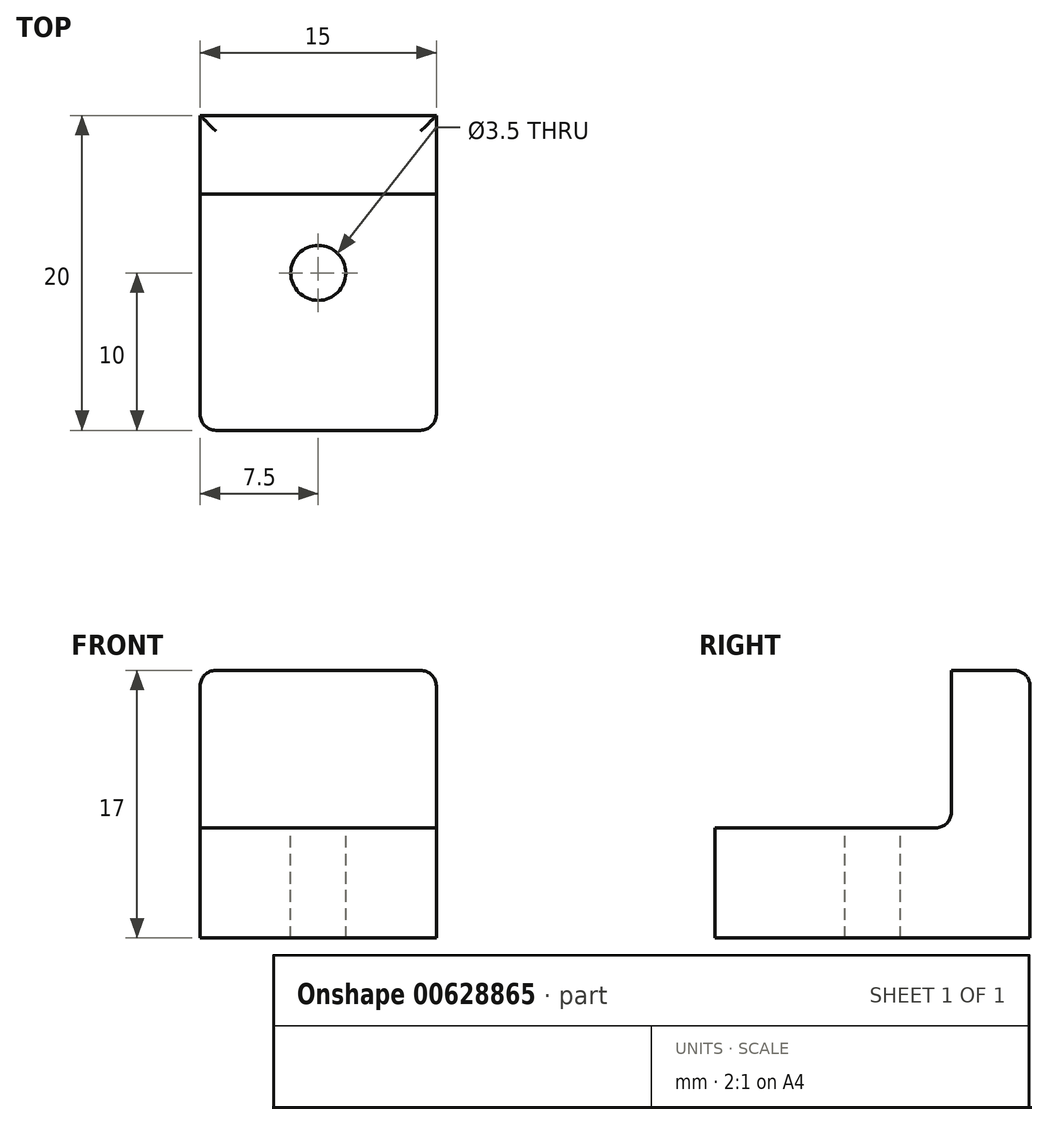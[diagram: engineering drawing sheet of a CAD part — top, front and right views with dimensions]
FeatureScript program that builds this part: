
annotation { "Feature Type Name" : "Feature", "Feature Type Description" : "" }
export const myFeature = defineFeature(function(context is Context, id is Id, definition is map)
    precondition{}
    {
        {
            var Q0;
            Q0=qCreatedBy(makeId("Top.planeOp"),FACE);
            var sketch = newSketch(context, id + "F0", { "sketchPlane" : qUnion([Q0])});
            skLineSegment(sketch, "E0.bottom", {"start": v(0, 0) * mm, "end": v(-15, 0) * mm});
            skLineSegment(sketch, "E0.top", {"start": v(0, 20) * mm, "end": v(-15, 20) * mm});
            skLineSegment(sketch, "E0.left", {"start": v(0, 0) * mm, "end": v(0, 20) * mm});
            skLineSegment(sketch, "E0.right", {"start": v(-15, 0) * mm, "end": v(-15, 20) * mm});
            skSolve(sketch);
        }
        {
            var Q0;
            Q0=qSketchRegion(id+"F0",true);
            extrude(context, id + "F1", {"entities" : qUnion([Q0]), "depth" : 17 * mm});
        }
        {
            var Q0;
            Q0=makeQuery(id+"F1.opExtrude","CAP_FACE",FACE,{"disambiguationData":[OSD([sQuery(id+"F0.wireOp",EDGE,"E0.bottom"),sQuery(id+"F0.wireOp",EDGE,"E0.top"),sQuery(id+"F0.wireOp",EDGE,"E0.left"),sQuery(id+"F0.wireOp",EDGE,"E0.right")])],"isStart":false});
            var sketch = newSketch(context, id + "F2", { "sketchPlane" : qUnion([Q0])});
            skLineSegment(sketch, "E1", {"start": v(0, 10) * mm, "end": v(-15, 10) * mm, "construction": true});
            skCircle(sketch, "E2", {"center": v(-7.5, 10) * mm, "radius": 1.75 * mm});
            skLineSegment(sketch, "E3", {"start": v(0, 15) * mm, "end": v(-15, 15) * mm});
            skSolve(sketch);
        }
        {
            var Q0;
            Q0=qSketchRegion(id+"F2",true);
            extrude(context, id + "F3", {"entities" : qUnion([Q0]), "operationType" : NewBodyOperationType.REMOVE, "endBound" : BoundingType.THROUGH_ALL, "oppositeDirection" : true, "depth" : 25 * mm});
        }
        {
            var Q0;
            Q0=makeQuery(id+"F2.imprint","IMPRINT",FACE,{"disambiguationData":[TD([[makeQuery(id+"F2.imprint","IMPRINT",EDGE,{"derivedFrom":sQuery(id+"F2.wireOp",EDGE,"E2")}),-1.0]])]});
            extrude(context, id + "F4", {"entities" : qUnion([Q0]), "operationType" : NewBodyOperationType.REMOVE, "oppositeDirection" : true, "depth" : 10 * mm});
        }
        {
            var Q0;
            Q0=makeQuery(id+"F1.opExtrude","CAP_EDGE",EDGE,{"disambiguationData":[OSD([sQuery(id+"F0.wireOp",EDGE,"E0.top")])],"isStart":false});
            var Q1;
            Q1=makeQuery(id+"F4.boolean.opBoolean","COPY",EDGE,{"derivedFrom":makeQuery(id+"F4.opExtrude","CAP_EDGE",EDGE,{"disambiguationData":[OSD([sQuery(id+"F2.wireOp",EDGE,"E3")])],"isStart":true})});
            var Q2;
            Q2=makeQuery(id+"F4.boolean.opBoolean","COPY",EDGE,{"derivedFrom":makeQuery(id+"F4.opExtrude","CAP_EDGE",EDGE,{"disambiguationData":[OSD([sQuery(id+"F2.wireOp",EDGE,"E3")])],"isStart":false})});
            var Q3;
            Q3=makeQuery(id+"F4.boolean.opBoolean","COPY",EDGE,{"derivedFrom":makeQuery(id+"F4.opExtrude","CAP_EDGE",EDGE,{"disambiguationData":[OSD([sQuery(id+"F0.wireOp",EDGE,"E0.bottom")])],"isStart":false})});
            var Q4;
            Q4=makeQuery(id+"F4.boolean.opBoolean","COPY",EDGE,{"derivedFrom":makeQuery(id+"F4.opExtrude","CAP_EDGE",EDGE,{"disambiguationData":[OSD([sQuery(id+"F0.wireOp",EDGE,"E0.right")])],"isStart":false})});
            var Q5;
            Q5=makeQuery(id+"F1.opExtrude","SWEPT_EDGE",EDGE,{"disambiguationData":[OSD([sQuery(id+"F0.wireOp",EDGE,"E0.bottom"),sQuery(id+"F0.wireOp",EDGE,"E0.right")])]});
            var Q6;
            Q6=makeQuery(id+"F4.boolean.opBoolean","COPY",EDGE,{"derivedFrom":makeQuery(id+"F4.opExtrude","SWEPT_EDGE",EDGE,{"disambiguationData":[OSD([sQuery(id+"F0.wireOp",EDGE,"E0.left"),sQuery(id+"F2.wireOp",EDGE,"E3")])]})});
            var Q7;
            Q7=makeQuery(id+"F1.opExtrude","SWEPT_EDGE",EDGE,{"disambiguationData":[OSD([sQuery(id+"F0.wireOp",EDGE,"E0.bottom"),sQuery(id+"F0.wireOp",EDGE,"E0.left")])]});
            var Q8;
            Q8=makeQuery(id+"F1.opExtrude","CAP_EDGE",EDGE,{"disambiguationData":[OSD([sQuery(id+"F0.wireOp",EDGE,"E0.left")])],"isStart":false});
            var Q9;
            Q9=makeQuery(id+"F1.opExtrude","CAP_EDGE",EDGE,{"disambiguationData":[OSD([sQuery(id+"F0.wireOp",EDGE,"E0.right")])],"isStart":false});
            fillet(context, id + "F5", {"entities" : qUnion([Q0, Q1, Q2, Q3, Q4, Q5, Q6, Q7, Q8, Q9]), "radius" : 1 * mm, "tangentPropagation" : true, "allowEdgeOverflow" : false});
        }
    });
